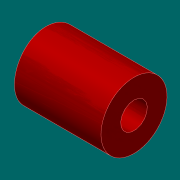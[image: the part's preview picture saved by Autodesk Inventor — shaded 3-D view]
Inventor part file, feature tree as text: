
AUTODESK INVENTOR PART (.ipt)
format: ipt  version: 2017.3 (Build 213257000, 257)  size: 143,360 bytes
history: native  units: in
note: dims shown in document units (in); Inventor stores cm internally (conversion verified against a paired STEP export)
features: sketch x2, revolve x1, fillet x1, extrude x1
ambient origin geometry x8: Origin, YZ Plane, XZ Plane, XY Plane, X Axis, Y Axis, Z Axis, Center Point
bodies: Solid1 (feature_tree)
feature tree (5):
  revolve  "Revolution1"  [1 undecoded]
  fillet  "Fillet1"  Radius=1.0in
  extrude  "Extrusion1"  TaperAngle=90.0deg  [1 undecoded]
  sketch  "Sketch1"  dims[d0=17.5in d1=2.4803in d2=1.0in]
  sketch  "Sketch2"  dims[d4=2.0in d7=90.0deg d8=0.0625in d9=28.5in d10=1.0in d11=0.0in]
note: 2 required parameter values undecoded (feature->parameter linkage not recoverable at this tier; creation-order binding heuristic only, values carry confidence <= 0.55)